# Revit family: Lighting-Proiezione-GEWISS-STADIUMPRO3-PROIETTORI-LED-ALTA-POTENZA_3MODULI
name_source: partatom
category: Apparecchi per illuminazione
units: mm (PartAtom-declared; Revit-internal decimal feet)

## family parameters
Condiviso = No
Host = Superficie
Punto di calcolo locali = Sì
Quota connettore circolare = Usa diametro
Sorgente d'illuminazione = Sì
Taglio con vuoti quando caricato = No
Tipo di parte = Normale

## types (1)
- Lighting-Proiezione-GEWISS-STADIUMPRO3-PROIETTORI-LED-ALTA-POTENZA_3MODULI
    Alimentatore = Da ordinare separatamente
    Angolo inclinazione = 60.00°
    Apparecchio a ridotta temperatura superficiale = -
    Applicazione = Interno / Esterno
    Cablaggio = Cavo multipolare tra proiettore e gruppo alimentazione
    Caratteristiche elettriche e gestione della luce = -
    Caratteristiche ottiche e illuminotecniche = -
    Catalogo = LIGHTING
    Certificazione DIN 18032-3 = -
    Certificazioni e classificazioni = -
    Classe fotobiologica = -
    Classe isolamento = I
    Classificazione: = -
    Codice digitale univoco (Datamatrix) = Attualmente non presente
    Colore = Grigio grafite
    Contesto = Illuminazione sportiva professionale
    Controllo abbagliamento e luminanza = ULOR = 0%
    Corpo = Alluminio pressofuso
    Descrizione = STADIUM PRO 3M CL.I C4 CRI 70 4000K
    Dispositivo di protezione = Secondo driver esterno
    Durata di vita = L90B10(Tq25°C)=40.000h; L80B10(Tq25°C)=75.000h
    Emetti da lunghezza linea = 610 mm
    Failure rate alimentatore = Secondo driver esterno
    File diagramma fotometrico = generic
    Filtro dei colori = 16777215
    Finitura colore = Verniciato a polvere poliestere
    Fissaggio = Staffa
    Frequenza nominale (Hz) = Secondo driver esterno
    Gancio di chiusura = -
    Garanzia = 5 anni
    Grado di protezione = IP66
    Gruppo ottico = lente T.I.R.Ex. in PMMA HT
    Guarnizioni = silicone antinvecchiamento
    IDF = b2048fe9-9939-4037-9b2b-b47a7e936639
    IDT = 0552d4b8-4f10-43b5-b8ac-94f59a03828d
    IPEA = STRADALE = A+ // GRANDI AREE = A3+ // CICLOPEDONALI = A++ // AREE VERDI = A++ // CENTRO STORICO = A5+ // ALTRO = A5+
    Immagine tipo = StadiumPro3.jpg
    Inclinazione = Rotazione su staffa con goniometro integrato
    Indice di resa cromatica = CRI70
    Informazioni generali = -
    Installazione e manutenzione = -
    Lugnezza massima = 74 mm  [stored 0.242782 ft]
    Materiali = -
    Modello = GWP3331AL740
    Norma di riferimento = EN60598-1; EN60598-2-5; IEC 62471; IEC 62778
    Ottica = Circolare 15°
    POSIZIONE = 80000
    Produttore = GEWISS S.p.A.
    Prospetto di default = 1219 mm
    Resistenza agli urti = IK08
    Resistenza al filo incandescente = -
    SEO = Proiettore
    Scheda Tecnica = https://www.gewiss.com
    Schermo = Vetro piano extrachiaro spessore 4mm
    Sistema di controllo = Secondo driver esterno
    Sostituibilità gruppo ottico = Non disponibile
    Sostituibilità piastra di cablaggio = Si
    Superficie massima esposta al vento : = 0,36 m2
    Temperatura di esercizio = -25 +50 °C
    Temperatura di stoccaggio = -
    Tensione di alimentazione = Secondo driver esterno
    Tipo di apparecchio = Proiettore LED ad alta potenza
    Tipo di installazione e montaggio = Torrefaro - Parete
    Tipologia sorgente luminosa = LED - Non sostituibile
    Tolleranza cromatica = SDCM = 5
    URL = https://www.gewiss.com
    Vano di alimentazione = Esterno
    Variazione temperatura colore lampada con luminosità attenuata = <Nessuno>
    Versione file RFA = 21.4
    Versioni = Luce naturale 4000K
    Viti esterne = Acciaio inossidabile
    larghezza lampada = 50 mm  [stored 0.164042 ft]

note: [stored X ft] marks values corroborated as IEEE doubles in the binary element streams (Revit-internal decimal feet)
